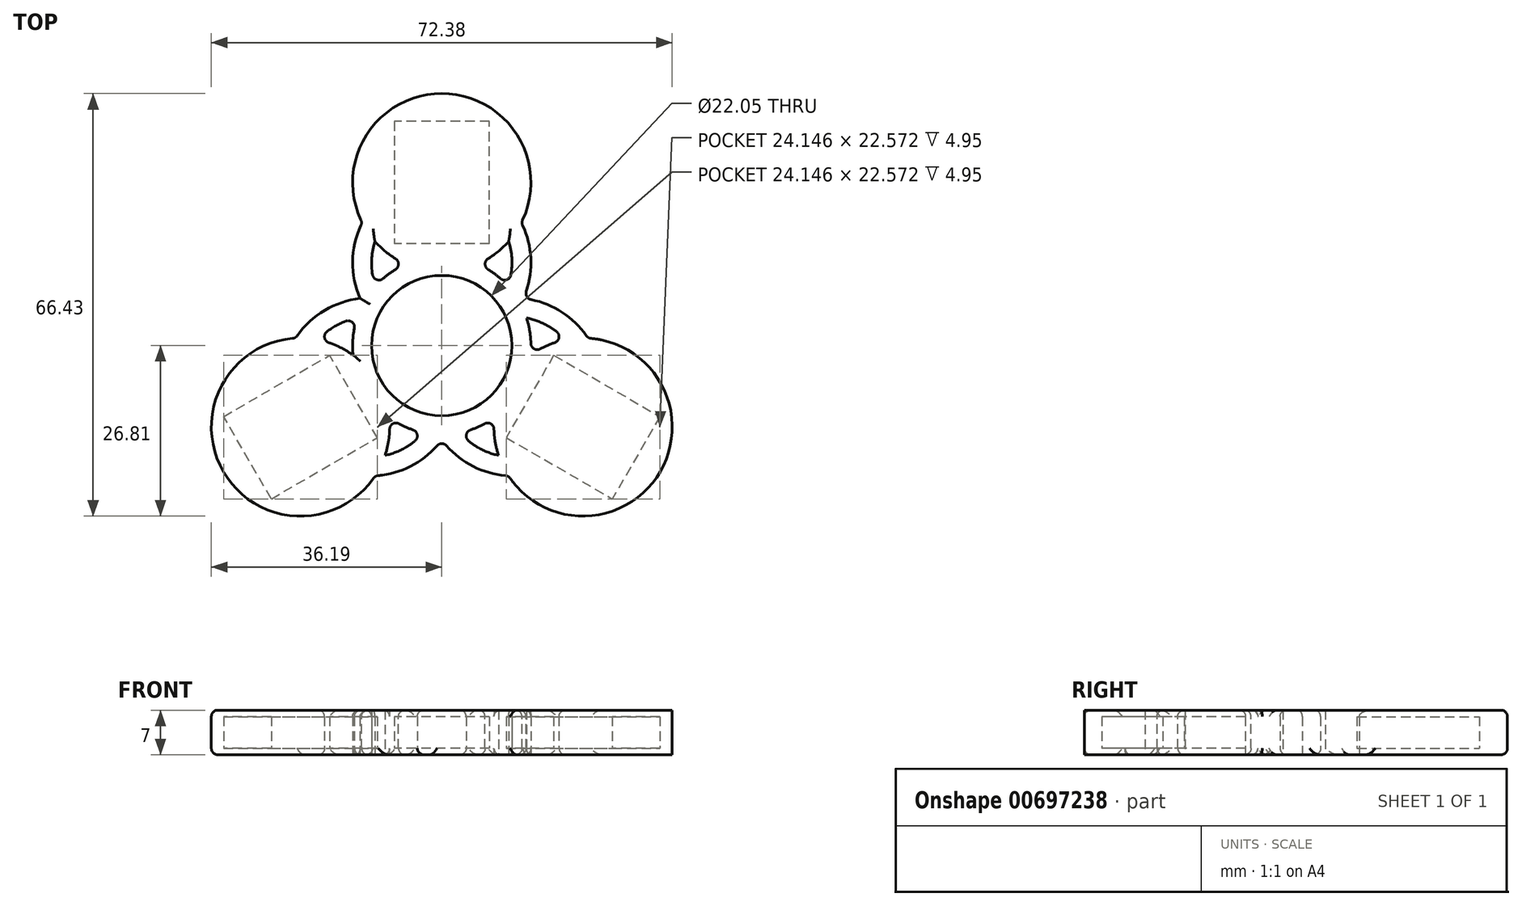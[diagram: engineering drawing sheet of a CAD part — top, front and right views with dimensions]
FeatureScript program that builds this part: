
annotation { "Feature Type Name" : "Feature", "Feature Type Description" : "" }
export const myFeature = defineFeature(function(context is Context, id is Id, definition is map)
    precondition{}
    {
        {
            var Q0;
            Q0=qCreatedBy(makeId("Top.planeOp"),FACE);
            var sketch = newSketch(context, id + "F0", { "sketchPlane" : qUnion([Q0])});
            skCircle(sketch, "E0", {"center": v(0, 0) * mm, "radius": 11.03 * mm});
            skCircle(sketch, "E1", {"center": v(0, 0) * mm, "radius": 14 * mm});
            skLineSegment(sketch, "E2.bottom", {"start": v(7.47, 16) * mm, "end": v(-7.48, 16) * mm});
            skLineSegment(sketch, "E2.top", {"start": v(7.48, 35.25) * mm, "end": v(-7.47, 35.25) * mm});
            skLineSegment(sketch, "E2.left", {"start": v(7.47, 16) * mm, "end": v(7.48, 35.25) * mm});
            skLineSegment(sketch, "E2.right", {"start": v(-7.48, 16) * mm, "end": v(-7.48, 35.25) * mm});
            skPoint(sketch, "E2.middle", {"position": v(0, 25.62) * mm});
            skCircle(sketch, "E3", {"center": v(0, 25.62) * mm, "radius": 14 * mm});
            skPoint(sketch, "E3.centerSnap0", {"position": v(0, 35.25) * mm});
            skCircle(sketch, "E4", {"center": v(0, 12.99) * mm, "radius": 11.03 * mm});
            skCircle(sketch, "E5", {"center": v(0, 12.99) * mm, "radius": 14 * mm});
            skCircle(sketch, "E6.1.0", {"center": v(-11.25, -6.5) * mm, "radius": 14 * mm});
            skCircle(sketch, "E6.1.1", {"center": v(-11.25, -6.5) * mm, "radius": 11.03 * mm});
            skCircle(sketch, "E6.1.2", {"center": v(-22.2, -12.81) * mm, "radius": 14 * mm});
            skLineSegment(sketch, "E6.1.3", {"start": v(-17.6, -1.53) * mm, "end": v(-10.12, -14.47) * mm});
            skLineSegment(sketch, "E6.1.4", {"start": v(-10.12, -14.47) * mm, "end": v(-26.79, -24.1) * mm});
            skLineSegment(sketch, "E6.1.5", {"start": v(-34.26, -11.15) * mm, "end": v(-26.79, -24.1) * mm});
            skLineSegment(sketch, "E6.1.6", {"start": v(-17.6, -1.53) * mm, "end": v(-34.26, -11.15) * mm});
            skCircle(sketch, "E6.2.0", {"center": v(11.25, -6.5) * mm, "radius": 14 * mm});
            skCircle(sketch, "E6.2.1", {"center": v(11.25, -6.5) * mm, "radius": 11.03 * mm});
            skCircle(sketch, "E6.2.2", {"center": v(22.2, -12.81) * mm, "radius": 14 * mm});
            skLineSegment(sketch, "E6.2.3", {"start": v(10.12, -14.47) * mm, "end": v(17.6, -1.53) * mm});
            skLineSegment(sketch, "E6.2.4", {"start": v(17.6, -1.53) * mm, "end": v(34.26, -11.15) * mm});
            skLineSegment(sketch, "E6.2.5", {"start": v(26.79, -24.1) * mm, "end": v(34.26, -11.15) * mm});
            skLineSegment(sketch, "E6.2.6", {"start": v(10.12, -14.47) * mm, "end": v(26.79, -24.1) * mm});
            skSolve(sketch);
        }
        {
            var Q0;
            Q0 = qSketchRegion(id + "F0", true);
            var Q1;
            {var subQ1=sQuery(id+"F0.wireOp",EDGE,"E2.bottom");Q1=makeQuery(id+"F0.imprint","IMPRINT",FACE,{"disambiguationData":[TD([[makeQuery(id+"F0.imprint","IMPRINT",EDGE,{"derivedFrom":subQ1}),1.0]])]});}
            var Q2;
            {var subQ11=sQuery(id+"F0.wireOp",EDGE,"E6.2.3");Q2=makeQuery(id+"F0.imprint","IMPRINT",FACE,{"disambiguationData":[TD([[makeQuery(id+"F0.imprint","IMPRINT",EDGE,{"derivedFrom":subQ11}),1.0]])]});}
            var Q3;
            {var subQ11=sQuery(id+"F0.wireOp",EDGE,"E6.1.3");Q3=makeQuery(id+"F0.imprint","IMPRINT",FACE,{"disambiguationData":[TD([[makeQuery(id+"F0.imprint","IMPRINT",EDGE,{"derivedFrom":subQ11}),1.0]])]});}
            var Q4;
            {var subQ0=sQuery(id+"F0.wireOp",EDGE,"E6.1.2");var subQ1=sQuery(id+"F0.wireOp",EDGE,"E1");var subQ2=makeQuery(id+"F0.imprint","INTERSECT",VERTEX,{"disambiguationData":[OD(0.0)],"derivedFrom":[subQ1,subQ0]});Q4=makeQuery(id+"F0.imprint","IMPRINT",FACE,{"disambiguationData":[TD([[makeQuery(id+"F0.imprint","IMPRINT",EDGE,{"disambiguationData":[TD([[subQ2,-1.0]])],"derivedFrom":subQ1}),1.0]])]});}
            var Q5;
            {var subQ0=sQuery(id+"F0.wireOp",EDGE,"E3");var subQ1=sQuery(id+"F0.wireOp",EDGE,"E1");var subQ2=makeQuery(id+"F0.imprint","INTERSECT",VERTEX,{"disambiguationData":[OD(0.0)],"derivedFrom":[subQ1,subQ0]});Q5=makeQuery(id+"F0.imprint","IMPRINT",FACE,{"disambiguationData":[TD([[makeQuery(id+"F0.imprint","IMPRINT",EDGE,{"disambiguationData":[TD([[subQ2,-1.0]])],"derivedFrom":subQ1}),1.0]])]});}
            var Q6;
            {var subQ0=sQuery(id+"F0.wireOp",EDGE,"E6.2.2");var subQ1=sQuery(id+"F0.wireOp",EDGE,"E1");var subQ2=makeQuery(id+"F0.imprint","INTERSECT",VERTEX,{"disambiguationData":[OD(0.0)],"derivedFrom":[subQ1,subQ0]});Q6=makeQuery(id+"F0.imprint","IMPRINT",FACE,{"disambiguationData":[TD([[makeQuery(id+"F0.imprint","IMPRINT",EDGE,{"disambiguationData":[TD([[subQ2,-1.0]])],"derivedFrom":subQ1}),1.0]])]});}
            var Q7;
            {var subQ0=sQuery(id+"F0.wireOp",EDGE,"E5");var subQ1=sQuery(id+"F0.wireOp",EDGE,"E0");var subQ2=makeQuery(id+"F0.imprint","INTERSECT",VERTEX,{"disambiguationData":[OD(0.0)],"derivedFrom":[subQ1,subQ0]});Q7=makeQuery(id+"F0.imprint","IMPRINT",FACE,{"disambiguationData":[TD([[makeQuery(id+"F0.imprint","IMPRINT",EDGE,{"disambiguationData":[TD([[subQ2,1.0]])],"derivedFrom":subQ1}),-1.0]])]});}
            var Q8;
            {var subQ0=sQuery(id+"F0.wireOp",EDGE,"E5");var subQ1=sQuery(id+"F0.wireOp",EDGE,"E1");var subQ2=makeQuery(id+"F0.imprint","INTERSECT",VERTEX,{"disambiguationData":[OD(0.0)],"derivedFrom":[subQ1,subQ0]});Q8=makeQuery(id+"F0.imprint","IMPRINT",FACE,{"disambiguationData":[TD([[makeQuery(id+"F0.imprint","IMPRINT",EDGE,{"disambiguationData":[TD([[subQ2,1.0]])],"derivedFrom":subQ1}),1.0]])]});}
            var Q9;
            {var subQ3=sQuery(id+"F0.wireOp",EDGE,"E6.2.1");var subQ5=sQuery(id+"F0.wireOp",EDGE,"E0");var subQ6=makeQuery(id+"F0.imprint","INTERSECT",VERTEX,{"disambiguationData":[OD(0.0)],"derivedFrom":[subQ5,subQ3]});Q9=makeQuery(id+"F0.imprint","IMPRINT",FACE,{"disambiguationData":[TD([[makeQuery(id+"F0.imprint","IMPRINT",EDGE,{"disambiguationData":[TD([[subQ6,-1.0]])],"derivedFrom":subQ5}),-1.0]])]});}
            var Q10;
            {var subQ0=sQuery(id+"F0.wireOp",EDGE,"E6.2.0");var subQ1=sQuery(id+"F0.wireOp",EDGE,"E1");var subQ2=makeQuery(id+"F0.imprint","INTERSECT",VERTEX,{"disambiguationData":[OD(0.0)],"derivedFrom":[subQ1,subQ0]});Q10=makeQuery(id+"F0.imprint","IMPRINT",FACE,{"disambiguationData":[TD([[makeQuery(id+"F0.imprint","IMPRINT",EDGE,{"disambiguationData":[TD([[subQ2,-1.0]])],"derivedFrom":subQ1}),1.0]])]});}
            var Q11;
            {var subQ7=sQuery(id+"F0.wireOp",EDGE,"E0");var subQ11=sQuery(id+"F0.wireOp",EDGE,"E6.2.0");var subQ12=makeQuery(id+"F0.imprint","INTERSECT",VERTEX,{"disambiguationData":[OD(0.0)],"derivedFrom":[subQ7,subQ11]});Q11=makeQuery(id+"F0.imprint","IMPRINT",FACE,{"disambiguationData":[TD([[makeQuery(id+"F0.imprint","IMPRINT",EDGE,{"disambiguationData":[TD([[subQ12,-1.0]])],"derivedFrom":subQ7}),-1.0]])]});}
            var Q12;
            {var subQ0=sQuery(id+"F0.wireOp",EDGE,"E4");var subQ1=sQuery(id+"F0.wireOp",EDGE,"E1");var subQ2=makeQuery(id+"F0.imprint","INTERSECT",VERTEX,{"disambiguationData":[OD(1.0)],"derivedFrom":[subQ1,subQ0]});Q12=makeQuery(id+"F0.imprint","IMPRINT",FACE,{"disambiguationData":[TD([[makeQuery(id+"F0.imprint","IMPRINT",EDGE,{"disambiguationData":[TD([[subQ2,-1.0]])],"derivedFrom":subQ1}),1.0]])]});}
            var Q13;
            {var subQ5=sQuery(id+"F0.wireOp",EDGE,"E4");var subQ6=sQuery(id+"F0.wireOp",EDGE,"E0");var subQ7=makeQuery(id+"F0.imprint","INTERSECT",VERTEX,{"disambiguationData":[OD(1.0)],"derivedFrom":[subQ6,subQ5]});Q13=makeQuery(id+"F0.imprint","IMPRINT",FACE,{"disambiguationData":[TD([[makeQuery(id+"F0.imprint","IMPRINT",EDGE,{"disambiguationData":[TD([[subQ7,-1.0]])],"derivedFrom":subQ6}),-1.0]])]});}
            var Q14;
            {var subQ0=sQuery(id+"F0.wireOp",EDGE,"E5");var subQ1=sQuery(id+"F0.wireOp",EDGE,"E1");var subQ2=makeQuery(id+"F0.imprint","INTERSECT",VERTEX,{"disambiguationData":[OD(1.0)],"derivedFrom":[subQ1,subQ0]});Q14=makeQuery(id+"F0.imprint","IMPRINT",FACE,{"disambiguationData":[TD([[makeQuery(id+"F0.imprint","IMPRINT",EDGE,{"disambiguationData":[TD([[subQ2,-1.0]])],"derivedFrom":subQ1}),1.0]])]});}
            var Q15;
            {var subQ7=sQuery(id+"F0.wireOp",EDGE,"E5");var subQ9=sQuery(id+"F0.wireOp",EDGE,"E0");var subQ10=makeQuery(id+"F0.imprint","INTERSECT",VERTEX,{"disambiguationData":[OD(1.0)],"derivedFrom":[subQ9,subQ7]});Q15=makeQuery(id+"F0.imprint","IMPRINT",FACE,{"disambiguationData":[TD([[makeQuery(id+"F0.imprint","IMPRINT",EDGE,{"disambiguationData":[TD([[subQ10,-1.0]])],"derivedFrom":subQ9}),-1.0]])]});}
            var Q16;
            {var subQ0=sQuery(id+"F0.wireOp",EDGE,"E6.1.1");var subQ1=sQuery(id+"F0.wireOp",EDGE,"E1");var subQ2=makeQuery(id+"F0.imprint","INTERSECT",VERTEX,{"disambiguationData":[OD(1.0)],"derivedFrom":[subQ1,subQ0]});Q16=makeQuery(id+"F0.imprint","IMPRINT",FACE,{"disambiguationData":[TD([[makeQuery(id+"F0.imprint","IMPRINT",EDGE,{"disambiguationData":[TD([[subQ2,-1.0]])],"derivedFrom":subQ1}),1.0]])]});}
            var Q17;
            {var subQ0=sQuery(id+"F0.wireOp",EDGE,"E6.1.1");var subQ1=sQuery(id+"F0.wireOp",EDGE,"E0");var subQ2=makeQuery(id+"F0.imprint","INTERSECT",VERTEX,{"disambiguationData":[OD(1.0)],"derivedFrom":[subQ1,subQ0]});Q17=makeQuery(id+"F0.imprint","IMPRINT",FACE,{"disambiguationData":[TD([[makeQuery(id+"F0.imprint","IMPRINT",EDGE,{"disambiguationData":[TD([[subQ2,-1.0]])],"derivedFrom":subQ1}),-1.0]])]});}
            var Q18;
            {var subQ0=sQuery(id+"F0.wireOp",EDGE,"E6.1.0");var subQ1=sQuery(id+"F0.wireOp",EDGE,"E1");var subQ2=makeQuery(id+"F0.imprint","INTERSECT",VERTEX,{"disambiguationData":[OD(1.0)],"derivedFrom":[subQ1,subQ0]});Q18=makeQuery(id+"F0.imprint","IMPRINT",FACE,{"disambiguationData":[TD([[makeQuery(id+"F0.imprint","IMPRINT",EDGE,{"disambiguationData":[TD([[subQ2,-1.0]])],"derivedFrom":subQ1}),1.0]])]});}
            var Q19;
            {var subQ0=sQuery(id+"F0.wireOp",EDGE,"E6.1.0");var subQ1=sQuery(id+"F0.wireOp",EDGE,"E0");var subQ2=makeQuery(id+"F0.imprint","INTERSECT",VERTEX,{"disambiguationData":[OD(0.0)],"derivedFrom":[subQ1,subQ0]});Q19=makeQuery(id+"F0.imprint","IMPRINT",FACE,{"disambiguationData":[TD([[makeQuery(id+"F0.imprint","IMPRINT",EDGE,{"disambiguationData":[TD([[subQ2,-1.0]])],"derivedFrom":subQ1}),-1.0]])]});}
            var Q20;
            {var subQ0=sQuery(id+"F0.wireOp",EDGE,"E6.1.1");var subQ1=sQuery(id+"F0.wireOp",EDGE,"E0");var subQ2=makeQuery(id+"F0.imprint","INTERSECT",VERTEX,{"disambiguationData":[OD(0.0)],"derivedFrom":[subQ1,subQ0]});Q20=makeQuery(id+"F0.imprint","IMPRINT",FACE,{"disambiguationData":[TD([[makeQuery(id+"F0.imprint","IMPRINT",EDGE,{"disambiguationData":[TD([[subQ2,-1.0]])],"derivedFrom":subQ1}),-1.0]])]});}
            var Q21;
            {var subQ0=sQuery(id+"F0.wireOp",EDGE,"E4");var subQ1=sQuery(id+"F0.wireOp",EDGE,"E0");var subQ2=makeQuery(id+"F0.imprint","INTERSECT",VERTEX,{"disambiguationData":[OD(0.0)],"derivedFrom":[subQ1,subQ0]});Q21=makeQuery(id+"F0.imprint","IMPRINT",FACE,{"disambiguationData":[TD([[makeQuery(id+"F0.imprint","IMPRINT",EDGE,{"disambiguationData":[TD([[subQ2,-1.0]])],"derivedFrom":subQ1}),-1.0]])]});}
            var Q22;
            {var subQ0=sQuery(id+"F0.wireOp",EDGE,"E6.2.1");var subQ1=sQuery(id+"F0.wireOp",EDGE,"E0");var subQ2=makeQuery(id+"F0.imprint","INTERSECT",VERTEX,{"disambiguationData":[OD(0.0)],"derivedFrom":[subQ1,subQ0]});Q22=makeQuery(id+"F0.imprint","IMPRINT",FACE,{"disambiguationData":[TD([[makeQuery(id+"F0.imprint","IMPRINT",EDGE,{"disambiguationData":[TD([[subQ2,1.0]])],"derivedFrom":subQ1}),-1.0]])]});}
            var Q23;
            {var subQ0=sQuery(id+"F0.wireOp",EDGE,"E6.2.1");var subQ1=sQuery(id+"F0.wireOp",EDGE,"E0");var subQ2=makeQuery(id+"F0.imprint","INTERSECT",VERTEX,{"disambiguationData":[OD(1.0)],"derivedFrom":[subQ1,subQ0]});Q23=makeQuery(id+"F0.imprint","IMPRINT",FACE,{"disambiguationData":[TD([[makeQuery(id+"F0.imprint","IMPRINT",EDGE,{"disambiguationData":[TD([[subQ2,-1.0]])],"derivedFrom":subQ1}),-1.0]])]});}
            var Q24;
            {var subQ0=sQuery(id+"F0.wireOp",EDGE,"E6.2.0");var subQ1=sQuery(id+"F0.wireOp",EDGE,"E0");var subQ2=makeQuery(id+"F0.imprint","INTERSECT",VERTEX,{"disambiguationData":[OD(1.0)],"derivedFrom":[subQ1,subQ0]});Q24=makeQuery(id+"F0.imprint","IMPRINT",FACE,{"disambiguationData":[TD([[makeQuery(id+"F0.imprint","IMPRINT",EDGE,{"disambiguationData":[TD([[subQ2,-1.0]])],"derivedFrom":subQ1}),-1.0]])]});}
            extrude(context, id + "F1", {"entities" : qUnion([Q0, Q1, Q2, Q3, Q4, Q5, Q6, Q7, Q8, Q9, Q10, Q11, Q12, Q13, Q14, Q15, Q16, Q17, Q18, Q19, Q20, Q21, Q22, Q23, Q24]), "depth" : 7 * mm, "offsetDistance" : 25 * mm});
        }
        {
            var Q0;
            Q0=makeQuery(id+"F1.opExtrude","SWEPT_FACE",FACE,{"disambiguationData":[OSD([sQuery(id+"F0.wireOp",EDGE,"E2.right")])]});
            var sketch = newSketch(context, id + "F2", { "sketchPlane" : qUnion([Q0])});
            skLineSegment(sketch, "E7.bottom", {"start": v(35.25, 0) * mm, "end": v(16, 0) * mm});
            skLineSegment(sketch, "E7.top", {"start": v(35.25, 1.03) * mm, "end": v(16, 1.02) * mm});
            skLineSegment(sketch, "E7.left", {"start": v(35.25, 0) * mm, "end": v(35.25, 1.03) * mm});
            skLineSegment(sketch, "E7.right", {"start": v(16, 0) * mm, "end": v(16, 1.02) * mm});
            skLineSegment(sketch, "E8.bottom", {"start": v(35.25, 7) * mm, "end": v(16, 7) * mm});
            skLineSegment(sketch, "E8.top", {"start": v(35.25, 5.98) * mm, "end": v(16, 5.97) * mm});
            skLineSegment(sketch, "E8.left", {"start": v(35.25, 7) * mm, "end": v(35.25, 5.97) * mm});
            skLineSegment(sketch, "E8.right", {"start": v(16, 7) * mm, "end": v(16, 5.97) * mm});
            skSolve(sketch);
        }
        {
            var Q0;
            Q0 = qSketchRegion(id + "F2", true);
            extrude(context, id + "F3", {"entities" : qUnion([Q0]), "operationType" : NewBodyOperationType.ADD, "endBound" : BoundingType.UP_TO_NEXT, "depth" : 7 * mm, "offsetDistance" : 25 * mm});
        }
        {
            var Q0;
            Q0=makeQuery(id+"F1.opExtrude","SWEPT_FACE",FACE,{"disambiguationData":[OSD([sQuery(id+"F0.wireOp",EDGE,"E6.1.6")])]});
            var sketch = newSketch(context, id + "F4", { "sketchPlane" : qUnion([Q0])});
            skLineSegment(sketch, "E9.bottom", {"start": v(-35.25, 0) * mm, "end": v(-16, 0) * mm});
            skLineSegment(sketch, "E9.top", {"start": v(-35.25, 1.02) * mm, "end": v(-16, 1.02) * mm});
            skLineSegment(sketch, "E9.left", {"start": v(-35.25, 0) * mm, "end": v(-35.25, 1.02) * mm});
            skLineSegment(sketch, "E9.right", {"start": v(-16, 0) * mm, "end": v(-16, 1.02) * mm});
            skLineSegment(sketch, "E10.bottom", {"start": v(-35.25, 7) * mm, "end": v(-16, 7) * mm});
            skLineSegment(sketch, "E10.top", {"start": v(-35.25, 5.98) * mm, "end": v(-16, 5.98) * mm});
            skLineSegment(sketch, "E10.left", {"start": v(-35.25, 7) * mm, "end": v(-35.25, 5.98) * mm});
            skLineSegment(sketch, "E10.right", {"start": v(-16, 7) * mm, "end": v(-16, 5.98) * mm});
            skSolve(sketch);
        }
        {
            var Q0;
            Q0 = qSketchRegion(id + "F4", true);
            extrude(context, id + "F5", {"entities" : qUnion([Q0]), "operationType" : NewBodyOperationType.ADD, "endBound" : BoundingType.UP_TO_NEXT, "depth" : 25 * mm, "offsetDistance" : 25 * mm});
        }
        {
            var Q0;
            Q0=makeQuery(id+"F1.opExtrude","SWEPT_FACE",FACE,{"disambiguationData":[OSD([sQuery(id+"F0.wireOp",EDGE,"E6.2.6")])]});
            var sketch = newSketch(context, id + "F6", { "sketchPlane" : qUnion([Q0])});
            skLineSegment(sketch, "E11.bottom", {"start": v(-16, 0) * mm, "end": v(-35.25, 0) * mm});
            skLineSegment(sketch, "E11.top", {"start": v(-16, 1.03) * mm, "end": v(-35.25, 1.02) * mm});
            skLineSegment(sketch, "E11.left", {"start": v(-16, 0) * mm, "end": v(-16, 1.03) * mm});
            skLineSegment(sketch, "E11.right", {"start": v(-35.25, 0) * mm, "end": v(-35.25, 1.02) * mm});
            skLineSegment(sketch, "E12.bottom", {"start": v(-16, 7) * mm, "end": v(-35.25, 7) * mm});
            skLineSegment(sketch, "E12.top", {"start": v(-16, 5.97) * mm, "end": v(-35.25, 5.97) * mm});
            skLineSegment(sketch, "E12.left", {"start": v(-16, 7) * mm, "end": v(-16, 5.97) * mm});
            skLineSegment(sketch, "E12.right", {"start": v(-35.25, 7) * mm, "end": v(-35.25, 5.97) * mm});
            skSolve(sketch);
        }
        {
            var Q0;
            Q0 = qSketchRegion(id + "F6", true);
            extrude(context, id + "F7", {"entities" : qUnion([Q0]), "operationType" : NewBodyOperationType.ADD, "endBound" : BoundingType.UP_TO_NEXT, "depth" : 25 * mm, "offsetDistance" : 25 * mm});
        }
        {
            var Q0;
            {var subQ0=sQuery(id+"F0.wireOp",EDGE,"E6.1.2");var subQ1=sQuery(id+"F0.wireOp",EDGE,"E6.1.0");Q0=makeQuery(id+"F1.opExtrude","CAP_EDGE",EDGE,{"disambiguationData":[OSD([subQ0]),TDD([makeQuery(id+"F0.imprint","IMPRINT",EDGE,{"disambiguationData":[TD([[makeQuery(id+"F0.imprint","INTERSECT",VERTEX,{"disambiguationData":[OD(0.0)],"derivedFrom":[subQ1,subQ0]}),-1.0]])],"derivedFrom":subQ0})])],"isStart":false});}
            var Q1;
            {var subQ0=sQuery(id+"F0.wireOp",EDGE,"E6.1.0");Q1=makeQuery(id+"F1.opExtrude","CAP_EDGE",EDGE,{"disambiguationData":[OSD([subQ0]),TDD([makeQuery(id+"F0.imprint","IMPRINT",EDGE,{"disambiguationData":[TD([[makeQuery(id+"F0.imprint","INTERSECT",VERTEX,{"disambiguationData":[OD(1.0)],"derivedFrom":[subQ0,sQuery(id+"F0.wireOp",EDGE,"E6.1.2")]}),-1.0]])],"derivedFrom":subQ0})])],"isStart":false});}
            var Q2;
            {var subQ0=sQuery(id+"F0.wireOp",EDGE,"E6.2.0");Q2=makeQuery(id+"F1.opExtrude","CAP_EDGE",EDGE,{"disambiguationData":[OSD([subQ0]),TDD([makeQuery(id+"F0.imprint","IMPRINT",EDGE,{"disambiguationData":[TD([[makeQuery(id+"F0.imprint","INTERSECT",VERTEX,{"disambiguationData":[OD(0.0)],"derivedFrom":[sQuery(id+"F0.wireOp",EDGE,"E6.1.0"),subQ0]}),-1.0]])],"derivedFrom":subQ0})])],"isStart":false});}
            var Q3;
            {var subQ0=sQuery(id+"F0.wireOp",EDGE,"E6.2.2");var subQ1=sQuery(id+"F0.wireOp",EDGE,"E6.2.0");Q3=makeQuery(id+"F1.opExtrude","CAP_EDGE",EDGE,{"disambiguationData":[OSD([subQ0]),TDD([makeQuery(id+"F0.imprint","IMPRINT",EDGE,{"disambiguationData":[TD([[makeQuery(id+"F0.imprint","INTERSECT",VERTEX,{"disambiguationData":[OD(0.0)],"derivedFrom":[subQ1,subQ0]}),-1.0]])],"derivedFrom":subQ0})])],"isStart":false});}
            var Q4;
            {var subQ0=sQuery(id+"F0.wireOp",EDGE,"E6.2.0");Q4=makeQuery(id+"F1.opExtrude","CAP_EDGE",EDGE,{"disambiguationData":[OSD([subQ0]),TDD([makeQuery(id+"F0.imprint","IMPRINT",EDGE,{"disambiguationData":[TD([[makeQuery(id+"F0.imprint","INTERSECT",VERTEX,{"disambiguationData":[OD(0.0)],"derivedFrom":[sQuery(id+"F0.wireOp",EDGE,"E5"),subQ0]}),1.0]])],"derivedFrom":subQ0})])],"isStart":false});}
            var Q5;
            {var subQ0=sQuery(id+"F0.wireOp",EDGE,"E5");Q5=makeQuery(id+"F1.opExtrude","CAP_EDGE",EDGE,{"disambiguationData":[OSD([subQ0]),TDD([makeQuery(id+"F0.imprint","IMPRINT",EDGE,{"disambiguationData":[TD([[makeQuery(id+"F0.imprint","INTERSECT",VERTEX,{"disambiguationData":[OD(1.0)],"derivedFrom":[sQuery(id+"F0.wireOp",EDGE,"E3"),subQ0]}),1.0]])],"derivedFrom":subQ0})])],"isStart":false});}
            var Q6;
            {var subQ0=sQuery(id+"F0.wireOp",EDGE,"E5");var subQ1=sQuery(id+"F0.wireOp",EDGE,"E3");Q6=makeQuery(id+"F1.opExtrude","CAP_EDGE",EDGE,{"disambiguationData":[OSD([subQ1]),TDD([makeQuery(id+"F0.imprint","IMPRINT",EDGE,{"disambiguationData":[TD([[makeQuery(id+"F0.imprint","INTERSECT",VERTEX,{"disambiguationData":[OD(0.0)],"derivedFrom":[subQ1,subQ0]}),1.0]])],"derivedFrom":subQ1})])],"isStart":false});}
            var Q7;
            {var subQ0=sQuery(id+"F0.wireOp",EDGE,"E5");Q7=makeQuery(id+"F1.opExtrude","CAP_EDGE",EDGE,{"disambiguationData":[OSD([subQ0]),TDD([makeQuery(id+"F0.imprint","IMPRINT",EDGE,{"disambiguationData":[TD([[makeQuery(id+"F0.imprint","INTERSECT",VERTEX,{"disambiguationData":[OD(0.0)],"derivedFrom":[sQuery(id+"F0.wireOp",EDGE,"E3"),subQ0]}),-1.0]])],"derivedFrom":subQ0})])],"isStart":false});}
            var Q8;
            {var subQ0=sQuery(id+"F0.wireOp",EDGE,"E6.1.0");Q8=makeQuery(id+"F1.opExtrude","CAP_EDGE",EDGE,{"disambiguationData":[OSD([subQ0]),TDD([makeQuery(id+"F0.imprint","IMPRINT",EDGE,{"disambiguationData":[TD([[makeQuery(id+"F0.imprint","INTERSECT",VERTEX,{"disambiguationData":[OD(0.0)],"derivedFrom":[sQuery(id+"F0.wireOp",EDGE,"E5"),subQ0]}),-1.0]])],"derivedFrom":subQ0})])],"isStart":false});}
            var Q9;
            {var subQ0=sQuery(id+"F0.wireOp",EDGE,"E1");Q9=makeQuery(id+"F1.opExtrude","CAP_EDGE",EDGE,{"disambiguationData":[OSD([subQ0]),TDD([makeQuery(id+"F0.imprint","IMPRINT",EDGE,{"disambiguationData":[TD([[makeQuery(id+"F0.imprint","INTERSECT",VERTEX,{"disambiguationData":[OD(0.0)],"derivedFrom":[subQ0,sQuery(id+"F0.wireOp",EDGE,"E6.1.1")]}),-1.0]])],"derivedFrom":subQ0})])],"isStart":false});}
            var Q10;
            {var subQ0=sQuery(id+"F0.wireOp",EDGE,"E3");Q10=makeQuery(id+"F1.opExtrude","CAP_EDGE",EDGE,{"disambiguationData":[OSD([subQ0]),TDD([makeQuery(id+"F0.imprint","IMPRINT",EDGE,{"disambiguationData":[TD([[makeQuery(id+"F0.imprint","INTERSECT",VERTEX,{"disambiguationData":[OD(1.0)],"derivedFrom":[sQuery(id+"F0.wireOp",EDGE,"E1"),subQ0]}),1.0]])],"derivedFrom":subQ0})])],"isStart":false});}
            var Q11;
            {var subQ0=sQuery(id+"F0.wireOp",EDGE,"E4");Q11=makeQuery(id+"F1.opExtrude","CAP_EDGE",EDGE,{"disambiguationData":[OSD([subQ0]),TDD([makeQuery(id+"F0.imprint","IMPRINT",EDGE,{"disambiguationData":[TD([[makeQuery(id+"F0.imprint","INTERSECT",VERTEX,{"disambiguationData":[OD(1.0)],"derivedFrom":[sQuery(id+"F0.wireOp",EDGE,"E1"),subQ0]}),1.0]])],"derivedFrom":subQ0})])],"isStart":false});}
            var Q12;
            {var subQ0=sQuery(id+"F0.wireOp",EDGE,"E1");Q12=makeQuery(id+"F1.opExtrude","CAP_EDGE",EDGE,{"disambiguationData":[OSD([subQ0]),TDD([makeQuery(id+"F0.imprint","IMPRINT",EDGE,{"disambiguationData":[TD([[makeQuery(id+"F0.imprint","INTERSECT",VERTEX,{"disambiguationData":[OD(1.0)],"derivedFrom":[subQ0,sQuery(id+"F0.wireOp",EDGE,"E3")]}),-1.0]])],"derivedFrom":subQ0})])],"isStart":false});}
            var Q13;
            {var subQ0=sQuery(id+"F0.wireOp",EDGE,"E4");Q13=makeQuery(id+"F1.opExtrude","CAP_EDGE",EDGE,{"disambiguationData":[OSD([subQ0]),TDD([makeQuery(id+"F0.imprint","IMPRINT",EDGE,{"disambiguationData":[TD([[makeQuery(id+"F0.imprint","INTERSECT",VERTEX,{"disambiguationData":[OD(0.0)],"derivedFrom":[sQuery(id+"F0.wireOp",EDGE,"E1"),subQ0]}),-1.0]])],"derivedFrom":subQ0})])],"isStart":false});}
            var Q14;
            {var subQ0=sQuery(id+"F0.wireOp",EDGE,"E3");Q14=makeQuery(id+"F1.opExtrude","CAP_EDGE",EDGE,{"disambiguationData":[OSD([subQ0]),TDD([makeQuery(id+"F0.imprint","IMPRINT",EDGE,{"disambiguationData":[TD([[makeQuery(id+"F0.imprint","INTERSECT",VERTEX,{"disambiguationData":[OD(0.0)],"derivedFrom":[sQuery(id+"F0.wireOp",EDGE,"E1"),subQ0]}),-1.0]])],"derivedFrom":subQ0})])],"isStart":false});}
            var Q15;
            {var subQ0=sQuery(id+"F0.wireOp",EDGE,"E1");Q15=makeQuery(id+"F1.opExtrude","CAP_EDGE",EDGE,{"disambiguationData":[OSD([subQ0]),TDD([makeQuery(id+"F0.imprint","IMPRINT",EDGE,{"disambiguationData":[TD([[makeQuery(id+"F0.imprint","INTERSECT",VERTEX,{"disambiguationData":[OD(0.0)],"derivedFrom":[subQ0,sQuery(id+"F0.wireOp",EDGE,"E4")]}),-1.0]])],"derivedFrom":subQ0})])],"isStart":false});}
            var Q16;
            {var subQ0=sQuery(id+"F0.wireOp",EDGE,"E6.2.2");Q16=makeQuery(id+"F1.opExtrude","SWEPT_FACE",FACE,{"disambiguationData":[OSD([subQ0]),TDD([makeQuery(id+"F0.imprint","IMPRINT",EDGE,{"disambiguationData":[TD([[makeQuery(id+"F0.imprint","INTERSECT",VERTEX,{"disambiguationData":[OD(1.0)],"derivedFrom":[sQuery(id+"F0.wireOp",EDGE,"E1"),subQ0]}),1.0]])],"derivedFrom":subQ0})])]});}
            var Q17;
            {var subQ0=sQuery(id+"F0.wireOp",EDGE,"E6.1.1");Q17=makeQuery(id+"F1.opExtrude","SWEPT_FACE",FACE,{"disambiguationData":[OSD([subQ0]),TDD([makeQuery(id+"F0.imprint","IMPRINT",EDGE,{"disambiguationData":[TD([[makeQuery(id+"F0.imprint","INTERSECT",VERTEX,{"disambiguationData":[OD(0.0)],"derivedFrom":[sQuery(id+"F0.wireOp",EDGE,"E1"),subQ0]}),-1.0]])],"derivedFrom":subQ0})])]});}
            var Q18;
            {var subQ0=sQuery(id+"F0.wireOp",EDGE,"E1");Q18=makeQuery(id+"F1.opExtrude","SWEPT_FACE",FACE,{"disambiguationData":[OSD([subQ0]),TDD([makeQuery(id+"F0.imprint","IMPRINT",EDGE,{"disambiguationData":[TD([[makeQuery(id+"F0.imprint","INTERSECT",VERTEX,{"disambiguationData":[OD(1.0)],"derivedFrom":[subQ0,sQuery(id+"F0.wireOp",EDGE,"E6.1.2")]}),-1.0]])],"derivedFrom":subQ0})])]});}
            var Q19;
            {var subQ0=sQuery(id+"F0.wireOp",EDGE,"E1");Q19=makeQuery(id+"F1.opExtrude","SWEPT_FACE",FACE,{"disambiguationData":[OSD([subQ0]),TDD([makeQuery(id+"F0.imprint","IMPRINT",EDGE,{"disambiguationData":[TD([[makeQuery(id+"F0.imprint","INTERSECT",VERTEX,{"disambiguationData":[OD(1.0)],"derivedFrom":[subQ0,sQuery(id+"F0.wireOp",EDGE,"E6.2.1")]}),-1.0]])],"derivedFrom":subQ0})])]});}
            var Q20;
            {var subQ0=sQuery(id+"F0.wireOp",EDGE,"E6.2.0");Q20=makeQuery(id+"F1.opExtrude","SWEPT_FACE",FACE,{"disambiguationData":[OSD([subQ0]),TDD([makeQuery(id+"F0.imprint","IMPRINT",EDGE,{"disambiguationData":[TD([[makeQuery(id+"F0.imprint","INTERSECT",VERTEX,{"disambiguationData":[OD(0.0)],"derivedFrom":[sQuery(id+"F0.wireOp",EDGE,"E6.1.0"),subQ0]}),-1.0]])],"derivedFrom":subQ0})])]});}
            var Q21;
            {var subQ0=sQuery(id+"F0.wireOp",EDGE,"E6.1.2");var subQ1=sQuery(id+"F0.wireOp",EDGE,"E6.1.0");Q21=makeQuery(id+"F1.opExtrude","SWEPT_FACE",FACE,{"disambiguationData":[OSD([subQ0]),TDD([makeQuery(id+"F0.imprint","IMPRINT",EDGE,{"disambiguationData":[TD([[makeQuery(id+"F0.imprint","INTERSECT",VERTEX,{"disambiguationData":[OD(0.0)],"derivedFrom":[subQ1,subQ0]}),-1.0]])],"derivedFrom":subQ0})])]});}
            var Q22;
            {var subQ0=sQuery(id+"F0.wireOp",EDGE,"E6.2.0");Q22=makeQuery(id+"F1.opExtrude","SWEPT_FACE",FACE,{"disambiguationData":[OSD([subQ0]),TDD([makeQuery(id+"F0.imprint","IMPRINT",EDGE,{"disambiguationData":[TD([[makeQuery(id+"F0.imprint","INTERSECT",VERTEX,{"disambiguationData":[OD(0.0)],"derivedFrom":[sQuery(id+"F0.wireOp",EDGE,"E5"),subQ0]}),1.0]])],"derivedFrom":subQ0})])]});}
            var Q23;
            {var subQ0=sQuery(id+"F0.wireOp",EDGE,"E5");var subQ1=sQuery(id+"F0.wireOp",EDGE,"E3");Q23=makeQuery(id+"F1.opExtrude","SWEPT_FACE",FACE,{"disambiguationData":[OSD([subQ1]),TDD([makeQuery(id+"F0.imprint","IMPRINT",EDGE,{"disambiguationData":[TD([[makeQuery(id+"F0.imprint","INTERSECT",VERTEX,{"disambiguationData":[OD(0.0)],"derivedFrom":[subQ1,subQ0]}),1.0]])],"derivedFrom":subQ1})])]});}
            var Q24;
            {var subQ0=sQuery(id+"F0.wireOp",EDGE,"E1");Q24=makeQuery(id+"F1.opExtrude","SWEPT_FACE",FACE,{"disambiguationData":[OSD([subQ0]),TDD([makeQuery(id+"F0.imprint","IMPRINT",EDGE,{"disambiguationData":[TD([[makeQuery(id+"F0.imprint","INTERSECT",VERTEX,{"disambiguationData":[OD(0.0)],"derivedFrom":[subQ0,sQuery(id+"F0.wireOp",EDGE,"E4")]}),-1.0]])],"derivedFrom":subQ0})])]});}
            var Q25;
            {var subQ0=sQuery(id+"F0.wireOp",EDGE,"E1");Q25=makeQuery(id+"F1.opExtrude","SWEPT_FACE",FACE,{"disambiguationData":[OSD([subQ0]),TDD([makeQuery(id+"F0.imprint","IMPRINT",EDGE,{"disambiguationData":[TD([[makeQuery(id+"F0.imprint","INTERSECT",VERTEX,{"disambiguationData":[OD(1.0)],"derivedFrom":[subQ0,sQuery(id+"F0.wireOp",EDGE,"E3")]}),-1.0]])],"derivedFrom":subQ0})])]});}
            fillet(context, id + "F8", {"entities" : qUnion([Q0, Q1, Q2, Q3, Q4, Q5, Q6, Q7, Q8, Q9, Q10, Q11, Q12, Q13, Q14, Q15, Q16, Q17, Q18, Q19, Q20, Q21, Q22, Q23, Q24, Q25]), "radius" : 1 * mm, "tangentPropagation" : true, "allowEdgeOverflow" : false});
        }
    });
